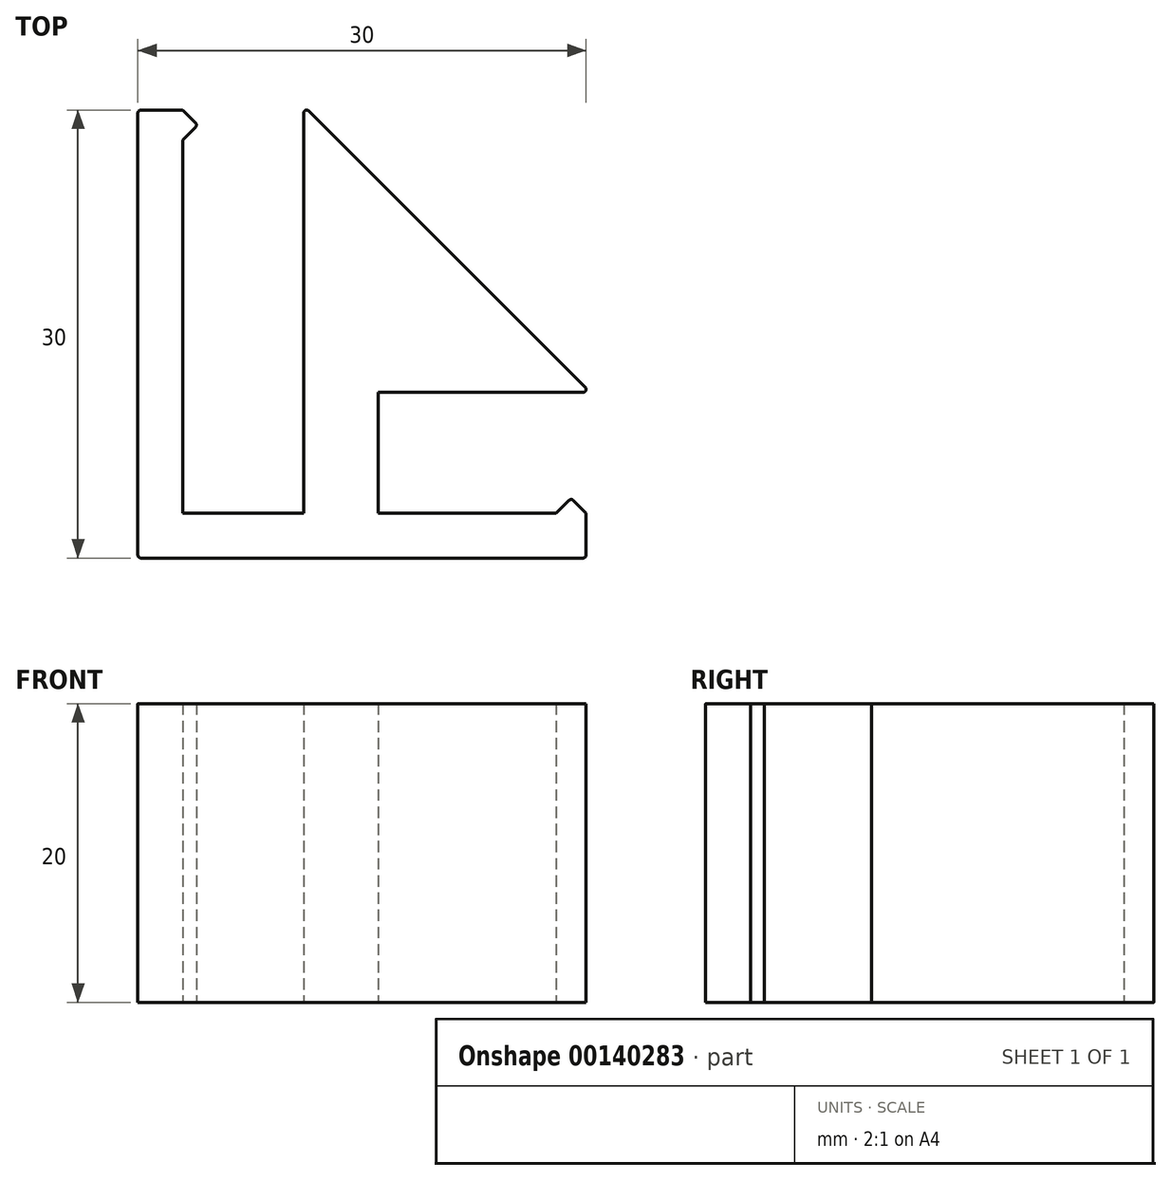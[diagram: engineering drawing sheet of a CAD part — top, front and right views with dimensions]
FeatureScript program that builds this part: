
annotation { "Feature Type Name" : "Feature", "Feature Type Description" : "" }
export const myFeature = defineFeature(function(context is Context, id is Id, definition is map)
    precondition{}
    {
        {
            var Q0;
            Q0=qCreatedBy(makeId("Top.planeOp"),FACE);
            var sketch = newSketch(context, id + "F0", { "sketchPlane" : qUnion([Q0])});
            skLineSegment(sketch, "E0.bottom", {"start": v(-51.16, 53.74) * mm, "end": v(-48.36, 53.74) * mm});
            skLineSegment(sketch, "E0.top", {"start": v(-51.16, 23.74) * mm, "end": v(-21.56, 23.74) * mm});
            skLineSegment(sketch, "E0.left", {"start": v(-51.36, 53.54) * mm, "end": v(-51.36, 23.94) * mm});
            skLineSegment(sketch, "E1.top", {"start": v(-48.36, 26.74) * mm, "end": v(-40.26, 26.74) * mm});
            skLineSegment(sketch, "E1.left", {"start": v(-48.36, 51.74) * mm, "end": v(-48.36, 26.74) * mm});
            skLineSegment(sketch, "E1.right", {"start": v(-40.26, 53.54) * mm, "end": v(-40.26, 26.74) * mm});
            skLineSegment(sketch, "E2.bottom", {"start": v(-23.36, 26.74) * mm, "end": v(-35.26, 26.74) * mm});
            skLineSegment(sketch, "E2.top", {"start": v(-21.56, 34.84) * mm, "end": v(-35.26, 34.84) * mm});
            skLineSegment(sketch, "E2.right", {"start": v(-35.26, 26.74) * mm, "end": v(-35.26, 34.84) * mm});
            skLineSegment(sketch, "E3.trimOffspring", {"start": v(-21.36, 26.74) * mm, "end": v(-21.36, 23.94) * mm});
            skLineSegment(sketch, "E4", {"start": v(-39.92, 53.68) * mm, "end": v(-21.42, 35.18) * mm});
            skLineSegment(sketch, "E5", {"start": v(-48.36, 53.74) * mm, "end": v(-47.5, 52.88) * mm});
            skLineSegment(sketch, "E6", {"start": v(-47.5, 52.6) * mm, "end": v(-48.36, 51.74) * mm});
            skLineSegment(sketch, "E7", {"start": v(-21.36, 26.74) * mm, "end": v(-22.22, 27.6) * mm});
            skLineSegment(sketch, "E8", {"start": v(-22.5, 27.6) * mm, "end": v(-23.36, 26.74) * mm});
            skPoint(sketch, "E9.visualSharp", {"position": v(-22.36, 27.74) * mm});
            skArc(sketch, "E9.filletArc", {"start": v(-22.22, 27.6) * mm, "mid": v(-22.36, 27.66) * mm, "end": v(-22.5, 27.6) * mm});
            skPoint(sketch, "E10.visualSharp", {"position": v(-47.36, 52.74) * mm});
            skArc(sketch, "E10.filletArc", {"start": v(-47.5, 52.6) * mm, "mid": v(-47.44, 52.74) * mm, "end": v(-47.5, 52.88) * mm});
            skPoint(sketch, "E11.visualSharp", {"position": v(-51.36, 53.74) * mm});
            skArc(sketch, "E11.filletArc", {"start": v(-51.16, 53.74) * mm, "mid": v(-51.3, 53.68) * mm, "end": v(-51.36, 53.54) * mm});
            skPoint(sketch, "E12.visualSharp", {"position": v(-51.36, 23.74) * mm});
            skArc(sketch, "E12.filletArc", {"start": v(-51.36, 23.94) * mm, "mid": v(-51.3, 23.8) * mm, "end": v(-51.16, 23.74) * mm});
            skPoint(sketch, "E13.visualSharp", {"position": v(-40.26, 54.02) * mm});
            skArc(sketch, "E13.filletArc", {"start": v(-39.92, 53.68) * mm, "mid": v(-40.13, 53.73) * mm, "end": v(-40.26, 53.54) * mm});
            skPoint(sketch, "E14.visualSharp", {"position": v(-21.36, 23.74) * mm});
            skArc(sketch, "E14.filletArc", {"start": v(-21.56, 23.74) * mm, "mid": v(-21.42, 23.8) * mm, "end": v(-21.36, 23.94) * mm});
            skPoint(sketch, "E15.visualSharp", {"position": v(-21.07, 34.84) * mm});
            skArc(sketch, "E15.filletArc", {"start": v(-21.56, 34.84) * mm, "mid": v(-21.37, 34.96) * mm, "end": v(-21.42, 35.18) * mm});
            skSolve(sketch);
        }
        {
            var Q0;
            Q0=makeQuery(id+"F0.imprint","IMPRINT",FACE,{"disambiguationData":[TD([[makeQuery(id+"F0.imprint","IMPRINT",EDGE,{"derivedFrom":sQuery(id+"F0.wireOp",EDGE,"E0.bottom")}),-1.0]])]});
            extrude(context, id + "F1", {"entities" : qUnion([Q0]), "depth" : 20 * mm});
        }
    });
